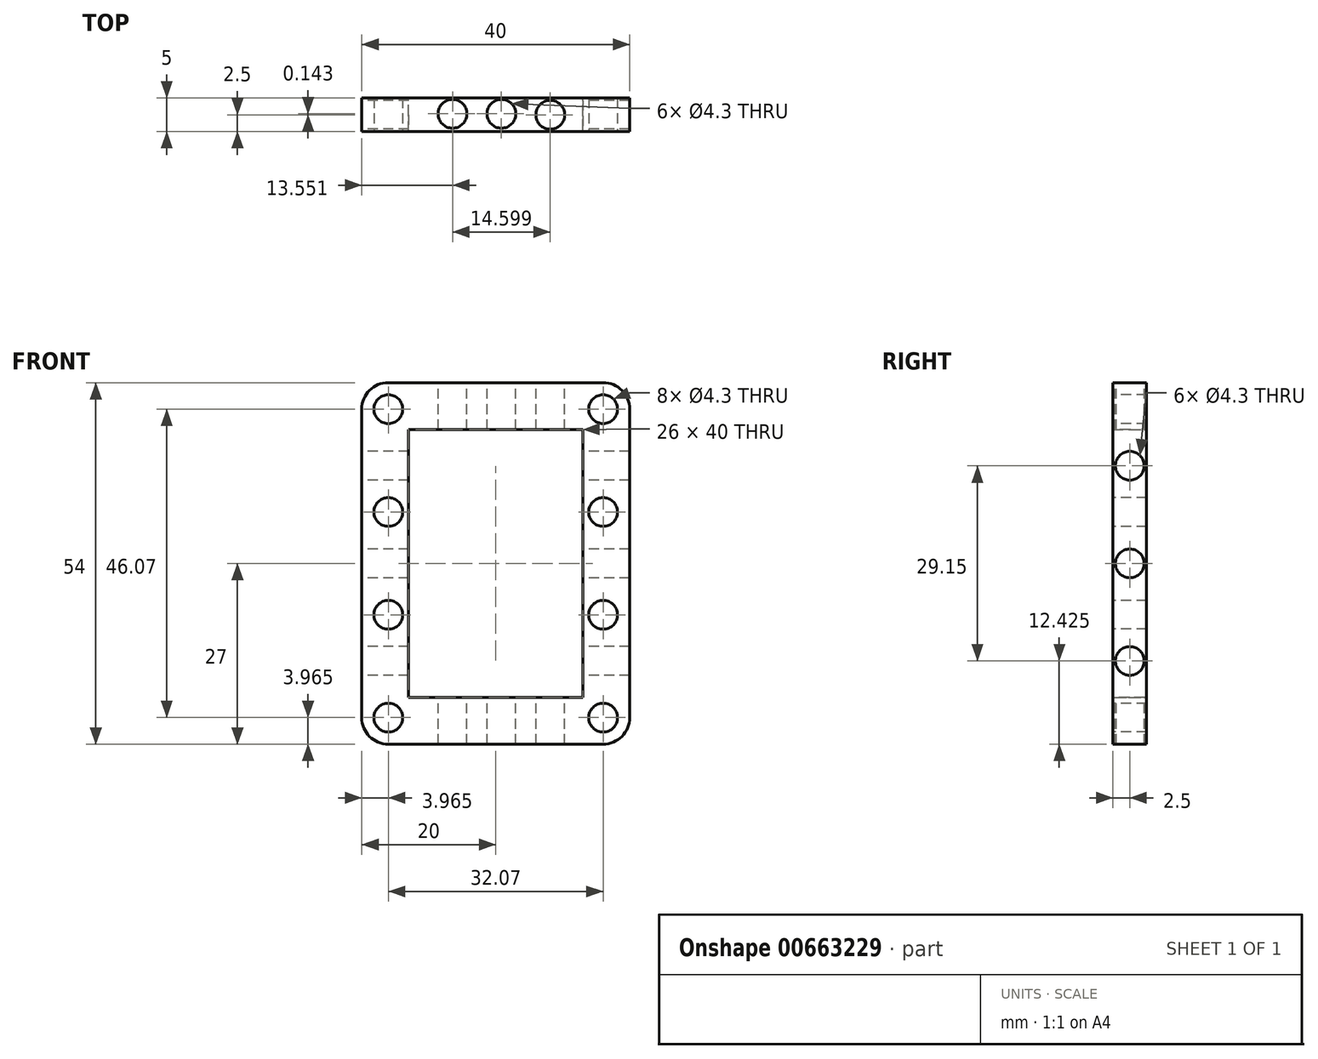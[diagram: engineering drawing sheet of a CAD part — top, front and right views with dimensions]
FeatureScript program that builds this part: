
annotation { "Feature Type Name" : "Feature", "Feature Type Description" : "" }
export const myFeature = defineFeature(function(context is Context, id is Id, definition is map)
    precondition{}
    {
        {
            var Q0;
            Q0=qCreatedBy(makeId("Front.planeOp"),FACE);
            var sketch = newSketch(context, id + "F0", { "sketchPlane" : qUnion([Q0])});
            skLineSegment(sketch, "E0.bottom", {"start": v(16.04, 27) * mm, "end": v(-16.04, 27) * mm});
            skLineSegment(sketch, "E0.top", {"start": v(16.03, -27) * mm, "end": v(-16.04, -27) * mm});
            skLineSegment(sketch, "E0.left", {"start": v(20, 23.04) * mm, "end": v(20, -23.04) * mm});
            skLineSegment(sketch, "E0.right", {"start": v(-20, 23.04) * mm, "end": v(-20, -23.04) * mm});
            skPoint(sketch, "E0.middle", {"position": v(0, 0) * mm});
            skLineSegment(sketch, "E1.bottom", {"start": v(13, 20) * mm, "end": v(-13, 20) * mm});
            skLineSegment(sketch, "E1.top", {"start": v(13, -20) * mm, "end": v(-13, -20) * mm});
            skLineSegment(sketch, "E1.left", {"start": v(13, 20) * mm, "end": v(13, -20) * mm});
            skLineSegment(sketch, "E1.right", {"start": v(-13, 20) * mm, "end": v(-13, -20) * mm});
            skPoint(sketch, "E2.visualSharp", {"position": v(20, 27) * mm});
            skArc(sketch, "E2.filletArc", {"start": v(20, 23.04) * mm, "mid": v(18.84, 25.84) * mm, "end": v(16.04, 27) * mm});
            skPoint(sketch, "E3.visualSharp", {"position": v(-20, 27) * mm});
            skArc(sketch, "E3.filletArc", {"start": v(-16.04, 27) * mm, "mid": v(-18.84, 25.84) * mm, "end": v(-20, 23.04) * mm});
            skPoint(sketch, "E4.visualSharp", {"position": v(-20, -27) * mm});
            skArc(sketch, "E4.filletArc", {"start": v(-20, -23.04) * mm, "mid": v(-18.84, -25.84) * mm, "end": v(-16.04, -27) * mm});
            skPoint(sketch, "E5.visualSharp", {"position": v(20, -27) * mm});
            skArc(sketch, "E5.filletArc", {"start": v(16.03, -27) * mm, "mid": v(18.84, -25.84) * mm, "end": v(20, -23.04) * mm});
            skSolve(sketch);
        }
        {
            var Q0;
            Q0 = qSketchRegion(id + "F0", true);
            extrude(context, id + "F1", {"entities" : qUnion([Q0]), "depth" : 5 * mm, "offsetDistance" : 25 * mm});
        }
        {
            var Q0;
            Q0=makeQuery(id+"F1.opExtrude","CAP_FACE",FACE,{"disambiguationData":[OSD([sQuery(id+"F0.wireOp",EDGE,"E0.bottom"),sQuery(id+"F0.wireOp",EDGE,"E0.top"),sQuery(id+"F0.wireOp",EDGE,"E0.left"),sQuery(id+"F0.wireOp",EDGE,"E0.right"),sQuery(id+"F0.wireOp",EDGE,"E1.bottom"),sQuery(id+"F0.wireOp",EDGE,"E1.top"),sQuery(id+"F0.wireOp",EDGE,"E1.left"),sQuery(id+"F0.wireOp",EDGE,"E1.right"),sQuery(id+"F0.wireOp",EDGE,"E2.filletArc"),sQuery(id+"F0.wireOp",EDGE,"E3.filletArc"),sQuery(id+"F0.wireOp",EDGE,"E4.filletArc"),sQuery(id+"F0.wireOp",EDGE,"E5.filletArc")])],"isStart":false});
            var sketch = newSketch(context, id + "F2", { "sketchPlane" : qUnion([Q0])});
            skCircle(sketch, "E6", {"center": v(-16.04, -23.04) * mm, "radius": 2.15 * mm});
            skCircle(sketch, "E7", {"center": v(-16.04, -7.68) * mm, "radius": 2.15 * mm});
            skCircle(sketch, "E8", {"center": v(-16.04, 7.68) * mm, "radius": 2.15 * mm});
            skCircle(sketch, "E9", {"center": v(-16.04, 23.04) * mm, "radius": 2.15 * mm});
            skCircle(sketch, "E10", {"center": v(16.04, 23.04) * mm, "radius": 2.15 * mm});
            skCircle(sketch, "E11", {"center": v(16.04, 7.68) * mm, "radius": 2.15 * mm});
            skCircle(sketch, "E12", {"center": v(16.04, -7.68) * mm, "radius": 2.15 * mm});
            skCircle(sketch, "E13", {"center": v(16.03, -23.04) * mm, "radius": 2.15 * mm});
            skSolve(sketch);
        }
        {
            var Q0;
            Q0 = qSketchRegion(id + "F2", true);
            extrude(context, id + "F3", {"entities" : qUnion([Q0]), "operationType" : NewBodyOperationType.REMOVE, "endBound" : BoundingType.THROUGH_ALL, "oppositeDirection" : true, "depth" : 25 * mm, "offsetDistance" : 25 * mm});
        }
        {
            var Q0;
            Q0=makeQuery(id+"F1.opExtrude","SWEPT_FACE",FACE,{"disambiguationData":[OSD([sQuery(id+"F0.wireOp",EDGE,"E0.bottom")])]});
            var sketch = newSketch(context, id + "F4", { "sketchPlane" : qUnion([Q0])});
            skCircle(sketch, "E14", {"center": v(8.15, -2.5) * mm, "radius": 2.15 * mm});
            skPoint(sketch, "E14.centerSnap0", {"position": v(16.04, -2.5) * mm});
            skCircle(sketch, "E15", {"center": v(0.85, -2.36) * mm, "radius": 2.15 * mm});
            skCircle(sketch, "E16", {"center": v(-6.45, -2.36) * mm, "radius": 2.15 * mm});
            skSolve(sketch);
        }
        {
            var Q0;
            Q0 = qSketchRegion(id + "F4", true);
            extrude(context, id + "F5", {"entities" : qUnion([Q0]), "operationType" : NewBodyOperationType.REMOVE, "endBound" : BoundingType.THROUGH_ALL, "oppositeDirection" : true, "depth" : 25 * mm, "offsetDistance" : 25 * mm});
        }
        {
            var Q0;
            Q0=makeQuery(id+"F1.opExtrude","SWEPT_FACE",FACE,{"disambiguationData":[OSD([sQuery(id+"F0.wireOp",EDGE,"E0.right")])]});
            var sketch = newSketch(context, id + "F6", { "sketchPlane" : qUnion([Q0])});
            skCircle(sketch, "E17", {"center": v(2.5, 14.58) * mm, "radius": 2.15 * mm});
            skPoint(sketch, "E17.centerSnap0", {"position": v(2.5, 23.04) * mm});
            skCircle(sketch, "E18", {"center": v(2.5, 0) * mm, "radius": 2.15 * mm});
            skCircle(sketch, "E19", {"center": v(2.5, -14.58) * mm, "radius": 2.15 * mm});
            skSolve(sketch);
        }
        {
            var Q0;
            Q0 = qSketchRegion(id + "F6", true);
            extrude(context, id + "F7", {"entities" : qUnion([Q0]), "operationType" : NewBodyOperationType.REMOVE, "endBound" : BoundingType.THROUGH_ALL, "oppositeDirection" : true, "depth" : 25 * mm, "offsetDistance" : 25 * mm});
        }
    });
